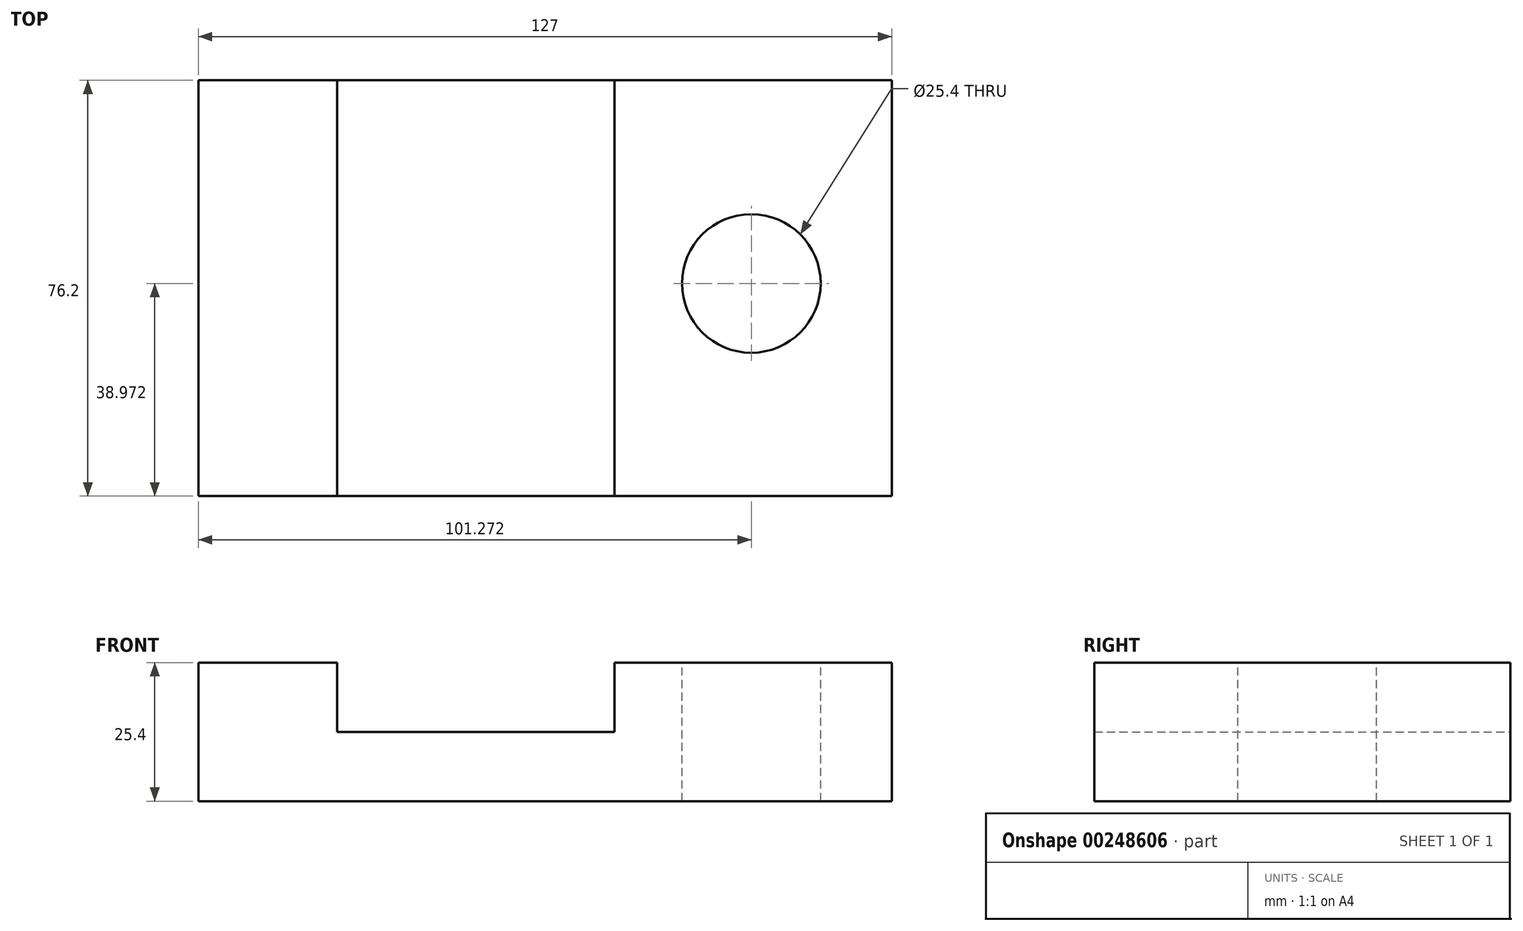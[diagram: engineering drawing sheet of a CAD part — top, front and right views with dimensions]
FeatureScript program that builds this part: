
annotation { "Feature Type Name" : "Feature", "Feature Type Description" : "" }
export const myFeature = defineFeature(function(context is Context, id is Id, definition is map)
    precondition{}
    {
        {
            var Q0;
            Q0=qCreatedBy(makeId("Top.planeOp"),FACE);
            var sketch = newSketch(context, id + "F0", { "sketchPlane" : qUnion([Q0])});
            skLineSegment(sketch, "E0.bottom", {"start": v(0, 0) * mm, "end": v(25.4, 0) * mm});
            skLineSegment(sketch, "E0.top", {"start": v(0, 76.2) * mm, "end": v(25.4, 76.2) * mm});
            skLineSegment(sketch, "E0.left", {"start": v(0, 0) * mm, "end": v(0, 76.2) * mm});
            skLineSegment(sketch, "E0.right", {"start": v(25.4, 0) * mm, "end": v(25.4, 76.2) * mm});
            skLineSegment(sketch, "E1.bottom", {"start": v(25.4, 0) * mm, "end": v(76.2, 0) * mm});
            skLineSegment(sketch, "E1.top", {"start": v(25.4, 76.2) * mm, "end": v(76.2, 76.2) * mm});
            skLineSegment(sketch, "E1.right", {"start": v(76.2, 0) * mm, "end": v(76.2, 76.2) * mm});
            skLineSegment(sketch, "E2.bottom", {"start": v(76.2, 0) * mm, "end": v(127, 0) * mm});
            skLineSegment(sketch, "E2.top", {"start": v(76.2, 76.2) * mm, "end": v(127, 76.2) * mm});
            skLineSegment(sketch, "E2.right", {"start": v(127, 0) * mm, "end": v(127, 76.2) * mm});
            skSolve(sketch);
        }
        {
            var Q0;
            Q0=makeQuery(id+"F0.imprint","IMPRINT",FACE,{"disambiguationData":[TD([[makeQuery(id+"F0.imprint","IMPRINT",EDGE,{"derivedFrom":sQuery(id+"F0.wireOp",EDGE,"E0.bottom")}),1.0]])]});
            extrude(context, id + "F1", {"entities" : qUnion([Q0]), "depth" : 25.4 * mm});
        }
        {
            var Q0;
            Q0=makeQuery(id+"F0.imprint","IMPRINT",FACE,{"disambiguationData":[TD([[makeQuery(id+"F0.imprint","IMPRINT",EDGE,{"derivedFrom":sQuery(id+"F0.wireOp",EDGE,"E1.bottom")}),1.0]])]});
            extrude(context, id + "F2", {"entities" : qUnion([Q0]), "operationType" : NewBodyOperationType.ADD, "depth" : 12.7 * mm});
        }
        {
            var Q0;
            Q0=makeQuery(id+"F0.imprint","IMPRINT",FACE,{"disambiguationData":[TD([[makeQuery(id+"F0.imprint","IMPRINT",EDGE,{"derivedFrom":sQuery(id+"F0.wireOp",EDGE,"E2.bottom")}),1.0]])]});
            extrude(context, id + "F3", {"entities" : qUnion([Q0]), "operationType" : NewBodyOperationType.ADD, "depth" : 25.4 * mm});
        }
        {
            var Q0;
            Q0=makeQuery(id+"F3.opExtrude","CAP_FACE",FACE,{"disambiguationData":[OSD([sQuery(id+"F0.wireOp",EDGE,"E2.bottom"),sQuery(id+"F0.wireOp",EDGE,"E2.top"),sQuery(id+"F0.wireOp",EDGE,"E1.right"),sQuery(id+"F0.wireOp",EDGE,"E2.right")])],"isStart":false});
            var sketch = newSketch(context, id + "F4", { "sketchPlane" : qUnion([Q0])});
            skPoint(sketch, "E3", {"position": v(101.27, 38.97) * mm});
            skSolve(sketch);
        }
        {
            var Q0;
            Q0=sQuery(id+"F4.wireOp",VERTEX,"E3");
            var Q1;
            Q1=makeQuery(id+"F1.opExtrude","SWEPT_BODY",BODY,{"disambiguationData":[OSD([sQuery(id+"F0.wireOp",EDGE,"E0.bottom"),sQuery(id+"F0.wireOp",EDGE,"E0.top"),sQuery(id+"F0.wireOp",EDGE,"E0.left"),sQuery(id+"F0.wireOp",EDGE,"E0.right")])]});
            hole(context, id + "F5", {"style" : HoleStyle.SIMPLE, "endStyle" : HoleEndStyle.THROUGH, "holeDiameter" : 25.4 * mm, "tappedDepth" : 12.7 * mm, "tapClearance" : 3, "locations" : qUnion([Q0]), "scope" : qUnion([Q1])});
        }
    });
